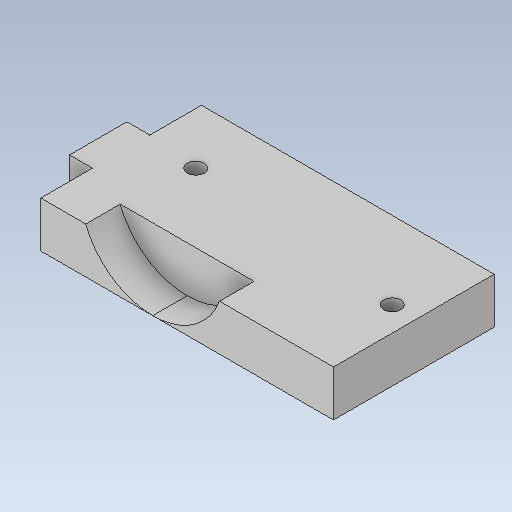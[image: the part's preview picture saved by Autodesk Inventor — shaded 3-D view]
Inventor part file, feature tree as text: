
AUTODESK INVENTOR PART (.ipt)
format: ipt  version: 2020.1 (Build 241239000, 239)  size: 153,088 bytes
history: native  units: mm
features: extrude x5, sketch x5, other x1
ambient origin geometry x8: Origin, YZ Plane, XZ Plane, XY Plane, X Axis, Y Axis, Z Axis, Center Point
bodies: Body1 (feature_tree)
feature tree (11):
  other  "Sólido1"
  extrude  "Extrusión1"  Depth=28.0mm
  extrude  "Extrusión2"  Depth=9.0mm
  extrude  "Extrusión3"  Depth=3.0mm
  extrude  "Extrusión4"  Depth=3.0mm
  extrude  "Extrusión5"  Depth=4.0mm
  sketch  "Boceto1"  dims[d0=51.0mm d1=28.0mm]
  sketch  "Boceto2"  dims[d2=18.5mm d3=9.0mm]
  sketch  "Boceto3"  dims[d4=3.0mm d5=14.5mm]
  sketch  "Boceto4"  dims[d6=4.25mm d7=3.0mm]
  sketch  "Boceto5"  dims[d8=14.0mm d9=4.0mm d10=5.0mm d11=5.0mm d12=2.0mm d13=0.0mm d14=2.0mm d15=0.0mm d16=6.0mm d17=0.0mm d18=9.0mm d19=9.0mm d20=3.0mm d21=8.0mm d22=0.0mm d23=25.0mm d24=23.5mm d25=6.0mm d26=0.0mm]
